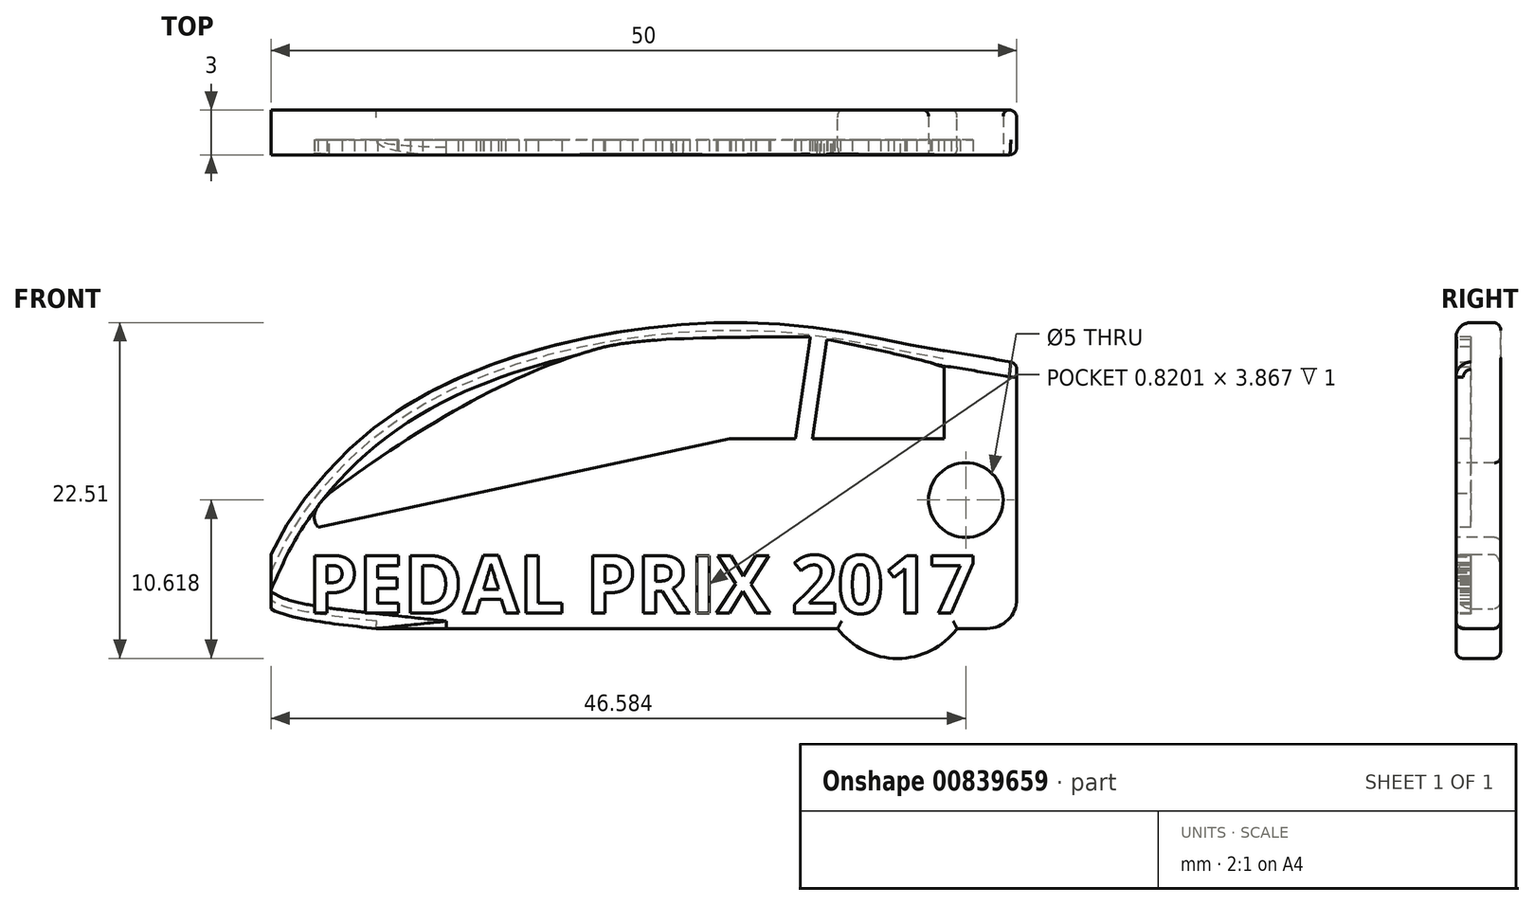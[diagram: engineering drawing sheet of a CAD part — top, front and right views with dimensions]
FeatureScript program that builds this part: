
annotation { "Feature Type Name" : "Feature", "Feature Type Description" : "" }
export const myFeature = defineFeature(function(context is Context, id is Id, definition is map)
    precondition{}
    {
        {
            var Q0;
            Q0=qCreatedBy(makeId("Front.planeOp"),FACE);
            var sketch = newSketch(context, id + "F0", { "sketchPlane" : qUnion([Q0])});
            skLineSegment(sketch, "E0.bottom", {"start": v(0, 0) * mm, "end": v(50, 0) * mm});
            skLineSegment(sketch, "E0.top", {"start": v(0, 25) * mm, "end": v(50, 25) * mm});
            skLineSegment(sketch, "E0.left", {"start": v(0, 0) * mm, "end": v(0, 25) * mm});
            skLineSegment(sketch, "E0.right", {"start": v(50, 0) * mm, "end": v(50, 25) * mm});
            skCircle(sketch, "E1", {"center": v(18, 3) * mm, "radius": 5 * mm});
            skCircle(sketch, "E2", {"center": v(42, 3) * mm, "radius": 5 * mm});
            skFitSpline(sketch, "E3", {"points": [v(50, 25) * mm, v(14.45, 25) * mm, v(6.92, 22.12) * mm], "startDerivative": vector(-62.35, 3.03) * mm, "endDerivative": vector(-18.65, -10.38) * mm});
            skFitSpline(sketch, "E4", {"points": [v(7.07, 0) * mm, v(0, 0) * mm], "startDerivative": vector(-7.07, 0) * mm, "endDerivative": vector(-7.07, 0) * mm});
            skFitSpline(sketch, "E5", {"points": [v(7.07, 0) * mm, v(0, 1.33) * mm, v(-0.7, 2.9) * mm, v(7.7, 14.04) * mm, v(34.38, 20.4) * mm, v(50, 18.35) * mm, v(63.02, 23.69) * mm], "startDerivative": vector(-67.46, 7.26) * mm, "endDerivative": vector(71.53, 41.01) * mm});
            skFitSpline(sketch, "E6", {"points": [v(45.07, 18.63) * mm, v(53.76, 16.69) * mm, v(54.7, 15.72) * mm], "startDerivative": vector(15.22, -2.42) * mm, "endDerivative": vector(2.1, -3.58) * mm});
            skSolve(sketch);
        }
        {
            var Q0;
            {var subQ0=sQuery(id+"F0.wireOp",EDGE,"E1");var subQ1=sQuery(id+"F0.wireOp",EDGE,"E0.bottom");var subQ2=makeQuery(id+"F0.imprint","INTERSECT",VERTEX,{"disambiguationData":[OD(0.0)],"derivedFrom":[subQ1,subQ0]});Q0=makeQuery(id+"F0.imprint","IMPRINT",FACE,{"disambiguationData":[TD([[makeQuery(id+"F0.imprint","IMPRINT",EDGE,{"disambiguationData":[TD([[subQ2,-1.0]])],"derivedFrom":subQ1}),1.0]])]});}
            var Q1;
            {var subQ0=sQuery(id+"F0.wireOp",EDGE,"E1");var subQ1=sQuery(id+"F0.wireOp",EDGE,"E0.bottom");var subQ2=makeQuery(id+"F0.imprint","INTERSECT",VERTEX,{"disambiguationData":[OD(0.0)],"derivedFrom":[subQ1,subQ0]});Q1=makeQuery(id+"F0.imprint","IMPRINT",FACE,{"disambiguationData":[TD([[makeQuery(id+"F0.imprint","IMPRINT",EDGE,{"disambiguationData":[TD([[subQ2,-1.0]])],"derivedFrom":subQ1}),-1.0]])]});}
            var Q2;
            {var subQ0=sQuery(id+"F0.wireOp",EDGE,"E2");var subQ1=sQuery(id+"F0.wireOp",EDGE,"E0.bottom");var subQ2=makeQuery(id+"F0.imprint","INTERSECT",VERTEX,{"disambiguationData":[OD(0.0)],"derivedFrom":[subQ1,subQ0]});Q2=makeQuery(id+"F0.imprint","IMPRINT",FACE,{"disambiguationData":[TD([[makeQuery(id+"F0.imprint","IMPRINT",EDGE,{"disambiguationData":[TD([[subQ2,-1.0]])],"derivedFrom":subQ1}),1.0]])]});}
            var Q3;
            {var subQ0=sQuery(id+"F0.wireOp",EDGE,"E2");var subQ1=sQuery(id+"F0.wireOp",EDGE,"E0.bottom");var subQ2=makeQuery(id+"F0.imprint","INTERSECT",VERTEX,{"disambiguationData":[OD(0.0)],"derivedFrom":[subQ1,subQ0]});Q3=makeQuery(id+"F0.imprint","IMPRINT",FACE,{"disambiguationData":[TD([[makeQuery(id+"F0.imprint","IMPRINT",EDGE,{"disambiguationData":[TD([[subQ2,-1.0]])],"derivedFrom":subQ1}),-1.0]])]});}
            var Q4;
            {var subQ0=sQuery(id+"F0.wireOp",EDGE,"E5");var subQ1=sQuery(id+"F0.wireOp",EDGE,"E0.left");var subQ2=makeQuery(id+"F0.imprint","INTERSECT",VERTEX,{"disambiguationData":[OD(0.0)],"derivedFrom":[subQ1,subQ0]});Q4=makeQuery(id+"F0.imprint","IMPRINT",FACE,{"disambiguationData":[TD([[makeQuery(id+"F0.imprint","IMPRINT",EDGE,{"disambiguationData":[TD([[subQ2,-1.0]])],"derivedFrom":subQ1}),1.0]])]});}
            var Q5;
            {var subQ5=sQuery(id+"F0.wireOp",EDGE,"E0.bottom");var subQ10=sQuery(id+"F0.wireOp",EDGE,"E1");var subQ11=makeQuery(id+"F0.imprint","INTERSECT",VERTEX,{"disambiguationData":[OD(1.0)],"derivedFrom":[subQ5,subQ10]});Q5=makeQuery(id+"F0.imprint","IMPRINT",FACE,{"disambiguationData":[TD([[makeQuery(id+"F0.imprint","IMPRINT",EDGE,{"disambiguationData":[TD([[subQ11,-1.0]])],"derivedFrom":subQ5}),1.0]])]});}
            extrude(context, id + "F1", {"entities" : qUnion([Q0, Q1, Q2, Q3, Q4, Q5]), "depth" : 3 * mm, "offsetDistance" : 25 * mm});
        }
        {
            var Q0;
            Q0=makeQuery(id+"F1.opExtrude","SWEPT_EDGE",EDGE,{"disambiguationData":[OSD([sQuery(id+"F0.wireOp",EDGE,"E0.bottom"),sQuery(id+"F0.wireOp",EDGE,"E0.right")])]});
            fillet(context, id + "F2", {"entities" : qUnion([Q0]), "radius" : 2 * mm, "tangentPropagation" : true, "allowEdgeOverflow" : false});
        }
        {
            var Q0;
            Q0=makeQuery(id+"F1.opExtrude","CAP_FACE",FACE,{"disambiguationData":[OSD([sQuery(id+"F0.wireOp",EDGE,"E0.bottom"),sQuery(id+"F0.wireOp",EDGE,"E0.right"),sQuery(id+"F0.wireOp",EDGE,"E1"),sQuery(id+"F0.wireOp",EDGE,"E2"),sQuery(id+"F0.wireOp",EDGE,"E5")])],"isStart":false});
            var sketch = newSketch(context, id + "F3", { "sketchPlane" : qUnion([Q0])});
            skFitSpline(sketch, "E7", {"points": [v(44.2, 17.84) * mm, v(17.48, 17.18) * mm, v(-11.42, -9.67) * mm, v(33.05, -8.35) * mm], "startDerivative": vector(-84.17, 20.62) * mm, "endDerivative": vector(176.36, 31.63) * mm});
            skFitSpline(sketch, "E8", {"points": [v(6.76, 11.11) * mm, v(3.17, 6.8) * mm, v(23.22, 5.63) * mm, v(21.17, 15.2) * mm], "startDerivative": vector(-29.49, -19.45) * mm, "endDerivative": vector(-22.62, 36.89) * mm});
            skLineSegment(sketch, "E9", {"start": v(3.17, 6.8) * mm, "end": v(30.75, 12.74) * mm});
            skLineSegment(sketch, "E10", {"start": v(30.75, 12.74) * mm, "end": v(45.12, 12.74) * mm});
            skLineSegment(sketch, "E11", {"start": v(45.12, 12.74) * mm, "end": v(45.12, 17.51) * mm});
            skLineSegment(sketch, "E12", {"start": v(45.12, 17.51) * mm, "end": v(44.2, 17.84) * mm});
            skLineSegment(sketch, "E13", {"start": v(36.3, 12.74) * mm, "end": v(37.26, 19.37) * mm});
            skLineSegment(sketch, "E14", {"start": v(35.16, 12.74) * mm, "end": v(36.2, 19.8) * mm});
            skFitSpline(sketch, "E15", {"points": [v(36.16, 19.55) * mm, v(21.21, 18.55) * mm, v(19.06, 16.91) * mm], "startDerivative": vector(-26.22, -0.04) * mm, "endDerivative": vector(-5.14, -6.04) * mm});
            skSolve(sketch);
        }
        {
            var Q0;
            {var subQ1=sQuery(id+"F3.wireOp",EDGE,"E8");var subQ3=sQuery(id+"F3.wireOp",EDGE,"E7");var subQ5=makeQuery(id+"F3.imprint","INTERSECT",VERTEX,{"disambiguationData":[OD(0.0)],"derivedFrom":[subQ3,subQ1]});Q0=makeQuery(id+"F3.imprint","IMPRINT",FACE,{"disambiguationData":[TD([[makeQuery(id+"F3.imprint","IMPRINT",EDGE,{"disambiguationData":[TD([[subQ5,1.0]])],"derivedFrom":subQ3}),1.0]])]});}
            var Q1;
            {var subQ1=sQuery(id+"F3.wireOp",EDGE,"E11");Q1=makeQuery(id+"F3.imprint","IMPRINT",FACE,{"disambiguationData":[TD([[makeQuery(id+"F3.imprint","IMPRINT",EDGE,{"derivedFrom":subQ1}),1.0]])]});}
            extrude(context, id + "F4", {"entities" : qUnion([Q0, Q1]), "operationType" : NewBodyOperationType.REMOVE, "oppositeDirection" : true, "depth" : 1 * mm, "offsetDistance" : 25 * mm});
        }
        {
            var Q0;
            Q0=makeQuery(id+"F1.opExtrude","CAP_FACE",FACE,{"disambiguationData":[OSD([sQuery(id+"F0.wireOp",EDGE,"E0.bottom"),sQuery(id+"F0.wireOp",EDGE,"E0.right"),sQuery(id+"F0.wireOp",EDGE,"E1"),sQuery(id+"F0.wireOp",EDGE,"E2"),sQuery(id+"F0.wireOp",EDGE,"E5")])],"isStart":false});
            var sketch = newSketch(context, id + "F5", { "sketchPlane" : qUnion([Q0])});
            skText(sketch, "E16", { "text": "PEDAL PRIX 2017", "fontName": "OpenSans-Bold.ttf"});
            const initialGuessF5  = {"E16": [0.00244, 0.00103, 1, 0, 0.0039]};
            skSetInitialGuess(sketch, initialGuessF5);
            skSolve(sketch);
        }
        {
            var Q0;
            Q0 = qSketchRegion(id + "F5", true);
            extrude(context, id + "F6", {"entities" : qUnion([Q0]), "operationType" : NewBodyOperationType.REMOVE, "oppositeDirection" : true, "depth" : 1 * mm, "offsetDistance" : 25 * mm});
        }
        {
            var Q0;
            {var subQ2=sQuery(id+"F0.wireOp",EDGE,"E0.right");var subQ3=sQuery(id+"F0.wireOp",EDGE,"E0.bottom");var subQ4=sQuery(id+"F0.wireOp",EDGE,"E2");var subQ7=sQuery(id+"F0.wireOp",EDGE,"E1");var subQ9=sQuery(id+"F0.wireOp",EDGE,"E5");Q0=makeQuery(id+"F6.boolean.opBoolean","SPLIT",FACE,{"disambiguationData":[TD([makeQuery(id+"F1.opExtrude","SWEPT_FACE",FACE,{"disambiguationData":[OSD([subQ2])]})])],"derivedFrom":makeQuery(id+"F1.opExtrude","CAP_FACE",FACE,{"disambiguationData":[OSD([subQ3,subQ2,subQ7,subQ4,subQ9])],"isStart":false})});}
            var sketch = newSketch(context, id + "F7", { "sketchPlane" : qUnion([Q0])});
            skCircle(sketch, "E17", {"center": v(46.58, 8.62) * mm, "radius": 2.5 * mm});
            skSolve(sketch);
        }
        {
            var Q0;
            Q0=makeQuery(id+"F7.imprint","IMPRINT",FACE,{"disambiguationData":[TD([[makeQuery(id+"F7.imprint","IMPRINT",EDGE,{"derivedFrom":sQuery(id+"F7.wireOp",EDGE,"P9eeZUrx-yCM7-GvIX-HcDr-smIq5cb4vAAc")}),1.0]])]});
            var Q1;
            Q1=makeQuery(id+"F7.imprint","IMPRINT",FACE,{"disambiguationData":[TD([[makeQuery(id+"F7.imprint","IMPRINT",EDGE,{"derivedFrom":sQuery(id+"F7.wireOp",EDGE,"E17")}),1.0]])]});
            extrude(context, id + "F8", {"entities" : qUnion([Q0, Q1]), "operationType" : NewBodyOperationType.REMOVE, "oppositeDirection" : true, "depth" : 25 * mm, "offsetDistance" : 25 * mm});
        }
        {
            var Q0;
            Q0=makeQuery(id+"F1.opExtrude","CAP_EDGE",EDGE,{"disambiguationData":[OSD([sQuery(id+"F0.wireOp",EDGE,"E5")])],"isStart":false});
            fillet(context, id + "F9", {"entities" : qUnion([Q0]), "radius" : 1 * mm, "tangentPropagation" : true, "allowEdgeOverflow" : false});
        }
        {
            var Q0;
            Q0=makeQuery(id+"F1.opExtrude","CAP_EDGE",EDGE,{"disambiguationData":[OSD([sQuery(id+"F0.wireOp",EDGE,"E5")])],"isStart":false});
            var Q1;
            Q1=makeQuery(id+"F1.opExtrude","CAP_EDGE",EDGE,{"disambiguationData":[OSD([sQuery(id+"F0.wireOp",EDGE,"E5")])],"isStart":true});
            var Q2;
            {var subQ0=sQuery(id+"F0.wireOp",EDGE,"E0.bottom");Q2=makeQuery(id+"F1.opExtrude","CAP_EDGE",EDGE,{"disambiguationData":[OSD([subQ0]),TDD([makeQuery(id+"F0.imprint","IMPRINT",EDGE,{"disambiguationData":[TD([[makeQuery(id+"F0.imprint","INTERSECT",VERTEX,{"disambiguationData":[OD(0.0)],"derivedFrom":[subQ0,sQuery(id+"F0.wireOp",EDGE,"E1")]}),1.0]])],"derivedFrom":subQ0})])],"isStart":true});}
            var Q3;
            {var subQ0=sQuery(id+"F0.wireOp",EDGE,"E0.bottom");Q3=makeQuery(id+"F1.opExtrude","CAP_EDGE",EDGE,{"disambiguationData":[OSD([subQ0]),TDD([makeQuery(id+"F0.imprint","IMPRINT",EDGE,{"disambiguationData":[TD([[makeQuery(id+"F0.imprint","INTERSECT",VERTEX,{"disambiguationData":[OD(1.0)],"derivedFrom":[subQ0,sQuery(id+"F0.wireOp",EDGE,"E1")]}),-1.0]])],"derivedFrom":subQ0})])],"isStart":true});}
            var Q4;
            {var subQ0=sQuery(id+"F0.wireOp",EDGE,"E0.bottom");Q4=makeQuery(id+"F1.opExtrude","CAP_EDGE",EDGE,{"disambiguationData":[OSD([subQ0]),TDD([makeQuery(id+"F0.imprint","IMPRINT",EDGE,{"disambiguationData":[TD([[makeQuery(id+"F0.imprint","INTERSECT",VERTEX,{"derivedFrom":[subQ0,sQuery(id+"F0.wireOp",EDGE,"E0.right")]}),1.0]])],"derivedFrom":subQ0})])],"isStart":true});}
            var Q5;
            Q5=makeQuery(id+"F1.opExtrude","CAP_EDGE",EDGE,{"disambiguationData":[OSD([sQuery(id+"F0.wireOp",EDGE,"E2")])],"isStart":true});
            var Q6;
            Q6=makeQuery(id+"F1.opExtrude","CAP_EDGE",EDGE,{"disambiguationData":[OSD([sQuery(id+"F0.wireOp",EDGE,"E1")])],"isStart":true});
            var Q7;
            Q7=makeQuery(id+"F1.opExtrude","CAP_EDGE",EDGE,{"disambiguationData":[OSD([sQuery(id+"F0.wireOp",EDGE,"E1")])],"isStart":false});
            var Q8;
            {var subQ0=sQuery(id+"F0.wireOp",EDGE,"E0.bottom");Q8=makeQuery(id+"F1.opExtrude","CAP_EDGE",EDGE,{"disambiguationData":[OSD([subQ0]),TDD([makeQuery(id+"F0.imprint","IMPRINT",EDGE,{"disambiguationData":[TD([[makeQuery(id+"F0.imprint","INTERSECT",VERTEX,{"disambiguationData":[OD(1.0)],"derivedFrom":[subQ0,sQuery(id+"F0.wireOp",EDGE,"E1")]}),-1.0]])],"derivedFrom":subQ0})])],"isStart":false});}
            var Q9;
            Q9=makeQuery(id+"F1.opExtrude","CAP_EDGE",EDGE,{"disambiguationData":[OSD([sQuery(id+"F0.wireOp",EDGE,"E2")])],"isStart":false});
            var Q10;
            {var subQ0=sQuery(id+"F0.wireOp",EDGE,"E0.bottom");Q10=makeQuery(id+"F1.opExtrude","CAP_EDGE",EDGE,{"disambiguationData":[OSD([subQ0]),TDD([makeQuery(id+"F0.imprint","IMPRINT",EDGE,{"disambiguationData":[TD([[makeQuery(id+"F0.imprint","INTERSECT",VERTEX,{"derivedFrom":[subQ0,sQuery(id+"F0.wireOp",EDGE,"E0.right")]}),1.0]])],"derivedFrom":subQ0})])],"isStart":false});}
            var Q11;
            {var subQ0=sQuery(id+"F0.wireOp",EDGE,"E0.bottom");Q11=makeQuery(id+"F1.opExtrude","CAP_EDGE",EDGE,{"disambiguationData":[OSD([subQ0]),TDD([makeQuery(id+"F0.imprint","IMPRINT",EDGE,{"disambiguationData":[TD([[makeQuery(id+"F0.imprint","INTERSECT",VERTEX,{"disambiguationData":[OD(0.0)],"derivedFrom":[subQ0,sQuery(id+"F0.wireOp",EDGE,"E1")]}),1.0]])],"derivedFrom":subQ0})])],"isStart":false});}
            fillet(context, id + "F10", {"entities" : qUnion([Q0, Q1, Q2, Q3, Q4, Q5, Q6, Q7, Q8, Q9, Q10, Q11]), "radius" : .5 * mm, "tangentPropagation" : true, "allowEdgeOverflow" : false});
        }
        {
            var Q0;
            Q0=makeQuery(id+"F8.boolean.opBoolean","COPY",EDGE,{"derivedFrom":makeQuery(id+"F8.opExtrude","CAP_EDGE",EDGE,{"disambiguationData":[OSD([sQuery(id+"F7.wireOp",EDGE,"E17")])],"isStart":true})});
            var Q1;
            Q1=makeQuery(id+"F8.boolean.opBoolean","INTERSECT",EDGE,{"derivedFrom":[makeQuery(id+"F1.opExtrude","CAP_FACE",FACE,{"disambiguationData":[OSD([sQuery(id+"F0.wireOp",EDGE,"E0.bottom"),sQuery(id+"F0.wireOp",EDGE,"E0.right"),sQuery(id+"F0.wireOp",EDGE,"E1"),sQuery(id+"F0.wireOp",EDGE,"E2"),sQuery(id+"F0.wireOp",EDGE,"E5"),sQuery(id+"F0.wireOp",EDGE,"E6")])],"isStart":true}),makeQuery(id+"F8.opExtrude","SWEPT_FACE",FACE,{"disambiguationData":[OSD([sQuery(id+"F7.wireOp",EDGE,"E17")])]})]});
            fillet(context, id + "F11", {"entities" : qUnion([Q0, Q1]), "radius" : .4 * mm, "tangentPropagation" : true, "allowEdgeOverflow" : false});
        }
    });
